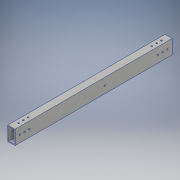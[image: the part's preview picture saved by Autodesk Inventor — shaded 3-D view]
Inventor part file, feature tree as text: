
AUTODESK INVENTOR PART (.ipt)
format: ipt  version: 2019 (Build 230136000, 136)  size: 176,640 bytes
history: native  units: mm
features: sketch x5, hole x3, extrude x2, other x1
ambient origin geometry x8: Origin, YZ Plane, XZ Plane, XY Plane, X Axis, Y Axis, Z Axis, Center Point
bodies: Body1 (feature_tree)
feature tree (11):
  other  "ソリッド1"
  extrude  "押し出し1"  Depth=15.0mm
  hole  "穴1"  [1 undecoded]
  hole  "穴2"  [1 undecoded]
  extrude  "押し出し2"  Depth=3.0mm
  hole  "穴3"  [1 undecoded]
  sketch  "スケッチ1"
  sketch  "スケッチ2"
  sketch  "スケッチ3"
  sketch  "スケッチ4"
  sketch  "スケッチ5"
note: 3 required parameter values undecoded (feature->parameter linkage not recoverable at this tier; creation-order binding heuristic only, values carry confidence <= 0.55)
